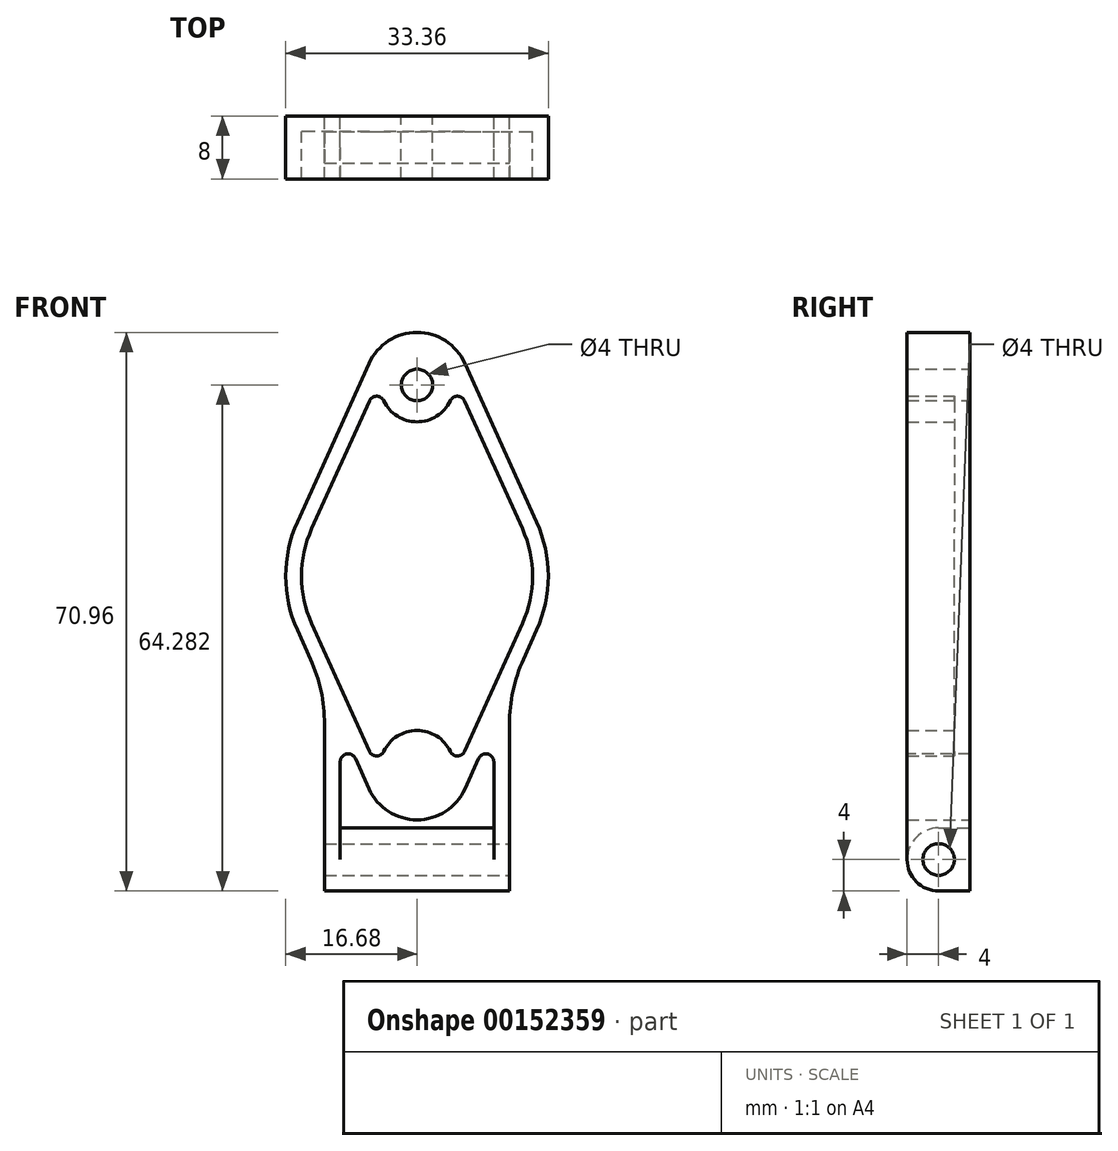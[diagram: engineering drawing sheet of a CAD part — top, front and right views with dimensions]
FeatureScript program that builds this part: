
annotation { "Feature Type Name" : "Feature", "Feature Type Description" : "" }
export const myFeature = defineFeature(function(context is Context, id is Id, definition is map)
    precondition{}
    {
        {
            var Q0;
            Q0=qCreatedBy(makeId("Front.planeOp"),FACE);
            var sketch = newSketch(context, id + "F0", { "sketchPlane" : qUnion([Q0])});
            skArc(sketch, "E0", {"start": v(6.09, 27.03) * mm, "mid": v(0, 30.96) * mm, "end": v(-6.09, 27.03) * mm});
            skArc(sketch, "E1.MirrorC", {"start": v(6.09, -27.03) * mm, "mid": v(0, -30.96) * mm, "end": v(-6.09, -27.03) * mm});
            skArc(sketch, "E2", {"start": v(-15.2, 6.86) * mm, "mid": v(-16.68, 0) * mm, "end": v(-15.2, -6.86) * mm});
            skLineSegment(sketch, "E3", {"start": v(-6.09, 27.03) * mm, "end": v(-15.2, 6.86) * mm});
            skLineSegment(sketch, "E4.MirrorCS", {"start": v(-6.09, -27.03) * mm, "end": v(-15.2, -6.86) * mm});
            skLineSegment(sketch, "E5.MirrorCS", {"start": v(6.09, 27.03) * mm, "end": v(15.2, 6.86) * mm});
            skLineSegment(sketch, "E6.MirrorCS", {"start": v(6.09, -27.03) * mm, "end": v(15.2, -6.86) * mm});
            skArc(sketch, "E7.trimOffspring", {"start": v(15.2, -6.86) * mm, "mid": v(16.68, 0) * mm, "end": v(15.2, 6.86) * mm});
            skCircle(sketch, "E8", {"center": v(0, 24.28) * mm, "radius": 2 * mm});
            skCircle(sketch, "E9.MirrorC", {"center": v(0, -24.28) * mm, "radius": 2 * mm});
            skLineSegment(sketch, "E10", {"start": v(-11.75, -14.5) * mm, "end": v(-11.75, -40) * mm});
            skLineSegment(sketch, "E11", {"start": v(-11.75, -40) * mm, "end": v(11.75, -40) * mm});
            skLineSegment(sketch, "E12", {"start": v(11.75, -40) * mm, "end": v(11.75, -14.5) * mm});
            skLineSegment(sketch, "E13.1", {"start": v(-6.05, 22.27) * mm, "end": v(-13.37, 6.04) * mm});
            skLineSegment(sketch, "E13.2", {"start": v(6.05, 22.27) * mm, "end": v(13.37, 6.04) * mm});
            skArc(sketch, "E13.3", {"start": v(-13.37, 6.04) * mm, "mid": v(-14.68, 0) * mm, "end": v(-13.37, -6.04) * mm});
            skArc(sketch, "E13.4", {"start": v(13.37, -6.04) * mm, "mid": v(14.68, 0) * mm, "end": v(13.37, 6.04) * mm});
            skLineSegment(sketch, "E13.5", {"start": v(6.05, -22.27) * mm, "end": v(13.37, -6.04) * mm});
            skLineSegment(sketch, "E13.7", {"start": v(-6.05, -22.27) * mm, "end": v(-13.37, -6.04) * mm});
            skLineSegment(sketch, "E14.0", {"start": v(9.75, -32) * mm, "end": v(9.75, -18.92) * mm});
            skLineSegment(sketch, "E14.2", {"start": v(-9.75, -18.92) * mm, "end": v(-9.75, -32) * mm});
            skArc(sketch, "E15", {"start": v(-4.23, 22.28) * mm, "mid": v(0, 19.6) * mm, "end": v(4.23, 22.28) * mm});
            skArc(sketch, "E16", {"start": v(4.23, -22.28) * mm, "mid": v(0, -19.6) * mm, "end": v(-4.23, -22.28) * mm});
            skPoint(sketch, "E17.visualSharp", {"position": v(-4.27, 26.2) * mm});
            skArc(sketch, "E17.filletArc", {"start": v(-4.23, 22.28) * mm, "mid": v(-5.14, 22.85) * mm, "end": v(-6.05, 22.27) * mm});
            skPoint(sketch, "E18.visualSharp", {"position": v(4.27, 26.2) * mm});
            skArc(sketch, "E18.filletArc", {"start": v(6.05, 22.27) * mm, "mid": v(5.14, 22.85) * mm, "end": v(4.23, 22.28) * mm});
            skPoint(sketch, "E19.visualSharp", {"position": v(4.27, -26.2) * mm});
            skArc(sketch, "E19.filletArc", {"start": v(4.23, -22.28) * mm, "mid": v(5.14, -22.85) * mm, "end": v(6.05, -22.27) * mm});
            skPoint(sketch, "E20.visualSharp", {"position": v(-4.27, -26.2) * mm});
            skArc(sketch, "E20.filletArc", {"start": v(-6.05, -22.27) * mm, "mid": v(-5.14, -22.85) * mm, "end": v(-4.23, -22.28) * mm});
            skLineSegment(sketch, "E21", {"start": v(-9.75, -32) * mm, "end": v(9.75, -32) * mm});
            skSolve(sketch);
        }
        {
            var Q0;
            Q0=makeQuery(id+"F0.imprint","IMPRINT",FACE,{"disambiguationData":[TD([[makeQuery(id+"F0.imprint","IMPRINT",EDGE,{"derivedFrom":sQuery(id+"F0.wireOp",EDGE,"E0")}),1.0]])]});
            var Q1;
            Q1=makeQuery(id+"F0.imprint","IMPRINT",FACE,{"disambiguationData":[TD([[makeQuery(id+"F0.imprint","IMPRINT",EDGE,{"derivedFrom":sQuery(id+"F0.wireOp",EDGE,"3e905b6d-8bee-4998-9225-6dcc00ec54d6.0")}),1.0]])]});
            var Q2;
            {var subQ0=sQuery(id+"F0.wireOp",EDGE,"E12");Q2=makeQuery(id+"F0.imprint","IMPRINT",FACE,{"disambiguationData":[TD([[makeQuery(id+"F0.imprint","IMPRINT",EDGE,{"derivedFrom":subQ0}),1.0]])]});}
            var Q3;
            {var subQ0=sQuery(id+"F0.wireOp",EDGE,"E10");Q3=makeQuery(id+"F0.imprint","IMPRINT",FACE,{"disambiguationData":[TD([[makeQuery(id+"F0.imprint","IMPRINT",EDGE,{"derivedFrom":subQ0}),1.0]])]});}
            var Q4;
            Q4=makeQuery(id+"F0.imprint","IMPRINT",FACE,{"disambiguationData":[TD([[makeQuery(id+"F0.imprint","IMPRINT",EDGE,{"derivedFrom":sQuery(id+"F0.wireOp",EDGE,"E9.MirrorC")}),1.0]])]});
            var Q5;
            Q5=makeQuery(id+"F0.imprint","IMPRINT",FACE,{"disambiguationData":[TD([[makeQuery(id+"F0.imprint","IMPRINT",EDGE,{"derivedFrom":sQuery(id+"F0.wireOp",EDGE,"E8")}),-1.0]])]});
            extrude(context, id + "F1", {"entities" : qUnion([Q0, Q1, Q2, Q3, Q4, Q5]), "depth" : 8 * mm});
        }
        {
            var Q0;
            {var subQ2=sQuery(id+"F0.wireOp",EDGE,"E13.1");Q0=makeQuery(id+"F0.imprint","IMPRINT",FACE,{"disambiguationData":[TD([[makeQuery(id+"F0.imprint","IMPRINT",EDGE,{"derivedFrom":subQ2}),1.0]])]});}
            var Q1;
            {var subQ1=sQuery(id+"F0.wireOp",EDGE,"E1.MirrorC");Q1=makeQuery(id+"F0.imprint","IMPRINT",FACE,{"disambiguationData":[TD([[makeQuery(id+"F0.imprint","IMPRINT",EDGE,{"derivedFrom":subQ1}),1.0]])]});}
            extrude(context, id + "F2", {"entities" : qUnion([Q0, Q1]), "operationType" : NewBodyOperationType.ADD, "depth" : 2 * mm});
        }
        {
            var Q0;
            Q0=makeQuery(id+"F1.opExtrude","SWEPT_EDGE",EDGE,{"disambiguationData":[OSD([sQuery(id+"F0.wireOp",EDGE,"E6.MirrorCS"),sQuery(id+"F0.wireOp",EDGE,"E12")])]});
            var Q1;
            Q1=makeQuery(id+"F1.opExtrude","SWEPT_EDGE",EDGE,{"disambiguationData":[OSD([sQuery(id+"F0.wireOp",EDGE,"E4.MirrorCS"),sQuery(id+"F0.wireOp",EDGE,"E10")])]});
            fillet(context, id + "F3", {"entities" : qUnion([Q0, Q1]), "radius" : 20 * mm, "tangentPropagation" : true, "allowEdgeOverflow" : false});
        }
        {
            var Q0;
            Q0=makeQuery(id+"F1.opExtrude","SWEPT_EDGE",EDGE,{"disambiguationData":[OSD([sQuery(id+"F0.wireOp",EDGE,"E6.MirrorCS"),sQuery(id+"F0.wireOp",EDGE,"E14.0")])]});
            var Q1;
            Q1=makeQuery(id+"F1.opExtrude","SWEPT_EDGE",EDGE,{"disambiguationData":[OSD([sQuery(id+"F0.wireOp",EDGE,"E4.MirrorCS"),sQuery(id+"F0.wireOp",EDGE,"E14.2")])]});
            fillet(context, id + "F4", {"entities" : qUnion([Q0, Q1]), "radius" : 1 * mm, "tangentPropagation" : true, "allowEdgeOverflow" : false});
        }
        {
            var Q0;
            Q0=makeQuery(id+"F1.opExtrude","SWEPT_FACE",FACE,{"disambiguationData":[OSD([sQuery(id+"F0.wireOp",EDGE,"E12")])]});
            var sketch = newSketch(context, id + "F5", { "sketchPlane" : qUnion([Q0])});
            skPoint(sketch, "E22", {"position": v(-4, -36) * mm});
            skLineSegment(sketch, "E23", {"start": v(-8, -40) * mm, "end": v(-4, -36) * mm, "construction": true});
            skLineSegment(sketch, "E24", {"start": v(-4, -36) * mm, "end": v(0, -40) * mm, "construction": true});
            skSolve(sketch);
        }
        {
            var Q0;
            Q0=sQuery(id+"F5.wireOp",VERTEX,"E22");
            var Q1;
            Q1=makeQuery(id+"F1.opExtrude","SWEPT_BODY",BODY,{"disambiguationData":[OSD([sQuery(id+"F0.wireOp",EDGE,"E0"),sQuery(id+"F0.wireOp",EDGE,"E2"),sQuery(id+"F0.wireOp",EDGE,"E3"),sQuery(id+"F0.wireOp",EDGE,"E5.MirrorCS"),sQuery(id+"F0.wireOp",EDGE,"E7.trimOffspring"),sQuery(id+"F0.wireOp",EDGE,"S2IiUO7s-7rjS-UU1n-G3Er-isHJvikYOna3"),sQuery(id+"F0.wireOp",EDGE,"U4xu2M48-wPnJ-tMoa-V4Px-PJSouQ81H8F5"),sQuery(id+"F0.wireOp",EDGE,"HV652KFt-d8Xn-WSbo-tHCJ-cfUj0g3Xd7DK"),sQuery(id+"F0.wireOp",EDGE,"E10"),sQuery(id+"F0.wireOp",EDGE,"E11"),sQuery(id+"F0.wireOp",EDGE,"E12"),sQuery(id+"F0.wireOp",EDGE,"W1IEodJy-6PRz-xiH1-2iNf-kAuRcIV7mYlj"),sQuery(id+"F0.wireOp",EDGE,"5ZKJKvnk-ET5z-qlB3-oLW5-LuLVHKlnV0HX"),sQuery(id+"F0.wireOp",EDGE,"Gk8awqwg-zgXA-VnUW-8MKI-QdblR6Wf13JX"),sQuery(id+"F0.wireOp",EDGE,"WIDdAYBM-okhh-eBsl-QBhJ-HuDdJqstO0Cl"),sQuery(id+"F0.wireOp",EDGE,"iXw4nrh7-EQqi-IiG2-VBaK-kNldmVsmUaTg"),sQuery(id+"F0.wireOp",EDGE,"03ff63bc-461f-42e4-a166-82e271801758"),sQuery(id+"F0.wireOp",EDGE,"5881da14-4dba-48e3-8e12-341ecdeeb7140.MirrorCS")])]});
            hole(context, id + "F6", {"style" : HoleStyle.SIMPLE, "endStyle" : HoleEndStyle.THROUGH, "standardTappedOrClearance" : lookupTablePath({ "standard" : "ISO", "size" : "4", "type" : "Drilled" }), "standardBlindInLast" : lookupTablePath({ "standard" : "ISO", "size" : "4", "type" : "Drilled" }), "holeDiameter" : 4 * mm, "locations" : qUnion([Q0]), "scope" : qUnion([Q1]), "isTappedThrough" : true});
        }
        {
            var Q0;
            {var subQ0=sQuery(id+"F0.wireOp",EDGE,"E11");Q0=makeQuery(id+"F1.opExtrude","CAP_EDGE",EDGE,{"disambiguationData":[OSD([subQ0]),TDD([makeQuery(id+"F0.imprint","IMPRINT",EDGE,{"disambiguationData":[TD([[makeQuery(id+"F0.imprint","INTERSECT",VERTEX,{"derivedFrom":[sQuery(id+"F0.wireOp",EDGE,"E10"),subQ0]}),-1.0]])],"derivedFrom":subQ0})])],"isStart":false});}
            var Q1;
            {var subQ0=sQuery(id+"F0.wireOp",EDGE,"E11");Q1=makeQuery(id+"F1.opExtrude","CAP_EDGE",EDGE,{"disambiguationData":[OSD([subQ0]),TDD([makeQuery(id+"F0.imprint","IMPRINT",EDGE,{"disambiguationData":[TD([[makeQuery(id+"F0.imprint","INTERSECT",VERTEX,{"derivedFrom":[subQ0,sQuery(id+"F0.wireOp",EDGE,"E12")]}),1.0]])],"derivedFrom":subQ0})])],"isStart":false});}
            var Q2;
            Q2=makeQuery(id+"F1.opExtrude","CAP_EDGE",EDGE,{"disambiguationData":[OSD([sQuery(id+"F0.wireOp",EDGE,"E21")])],"isStart":false});
            fillet(context, id + "F7", {"entities" : qUnion([Q0, Q1, Q2]), "radius" : (8 / 2) * mm, "tangentPropagation" : true, "allowEdgeOverflow" : false});
        }
    });
